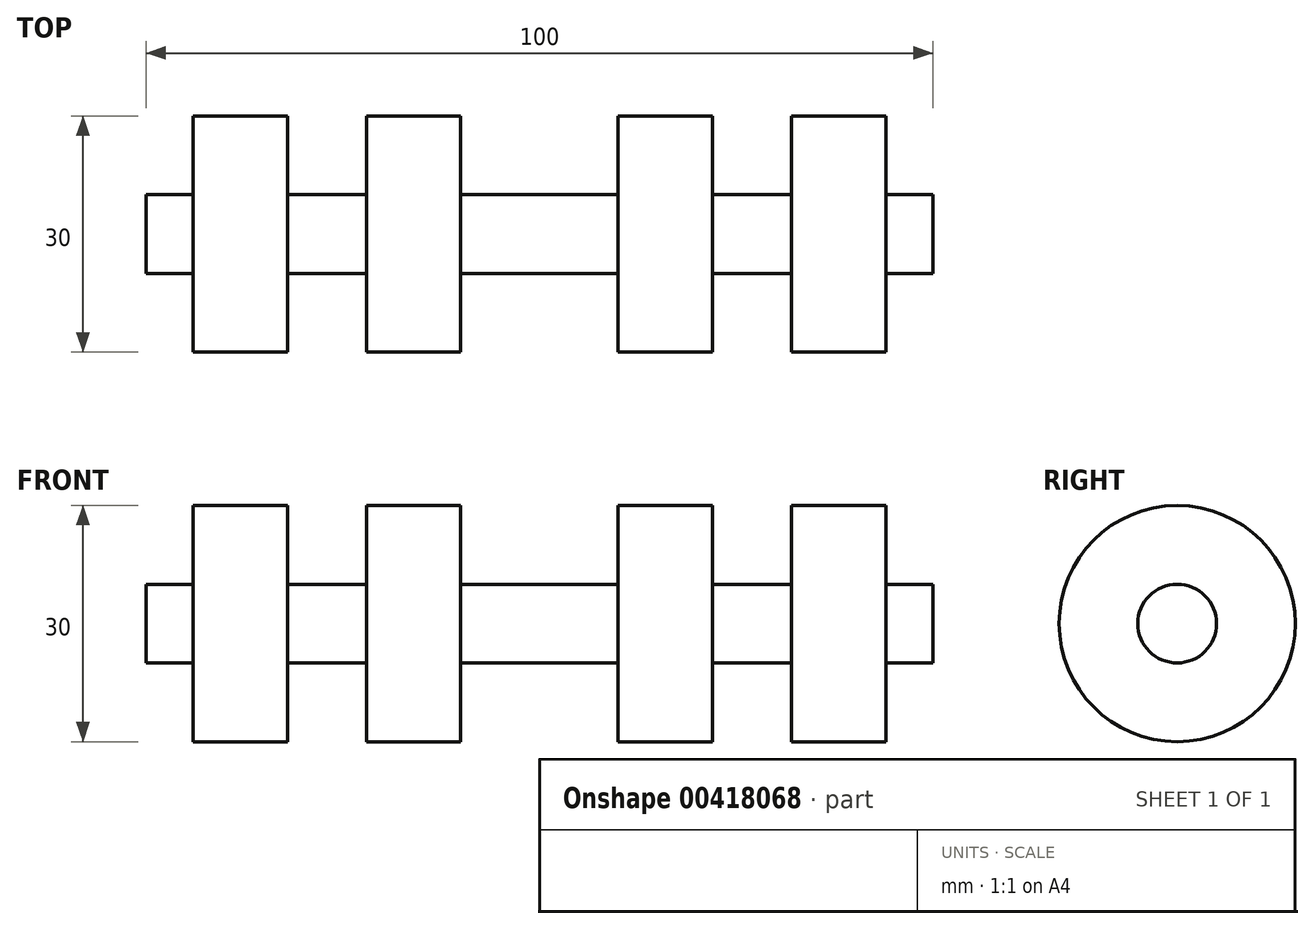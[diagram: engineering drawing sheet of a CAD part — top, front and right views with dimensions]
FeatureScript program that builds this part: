
annotation { "Feature Type Name" : "Feature", "Feature Type Description" : "" }
export const myFeature = defineFeature(function(context is Context, id is Id, definition is map)
    precondition{}
    {
        {
            var Q0;
            Q0=qCreatedBy(makeId("Front.planeOp"),FACE);
            var sketch = newSketch(context, id + "F0", { "sketchPlane" : qUnion([Q0])});
            skLineSegment(sketch, "E0.bottom", {"start": v(0, 0) * mm, "end": v(-100, 0) * mm});
            skLineSegment(sketch, "E0.top", {"start": v(-6, 15) * mm, "end": v(-18, 15) * mm});
            skLineSegment(sketch, "E0.left", {"start": v(0, 0) * mm, "end": v(0, 5) * mm});
            skLineSegment(sketch, "E0.right", {"start": v(-100, 0) * mm, "end": v(-100, 5) * mm});
            skLineSegment(sketch, "E1", {"start": v(-100, 5) * mm, "end": v(-94, 5) * mm});
            skLineSegment(sketch, "E2", {"start": v(-94, 15) * mm, "end": v(-94, 5) * mm});
            skLineSegment(sketch, "E3", {"start": v(-6, 15) * mm, "end": v(-6, 5) * mm});
            skLineSegment(sketch, "E4", {"start": v(-82, 15) * mm, "end": v(-82, 5) * mm});
            skLineSegment(sketch, "E5", {"start": v(-72, 15) * mm, "end": v(-72, 5) * mm});
            skLineSegment(sketch, "E6", {"start": v(-28, 15) * mm, "end": v(-28, 5) * mm});
            skLineSegment(sketch, "E7", {"start": v(-18, 15) * mm, "end": v(-18, 5) * mm});
            skLineSegment(sketch, "E8.trimOffspring", {"start": v(-6, 5) * mm, "end": v(0, 5) * mm});
            skLineSegment(sketch, "E9.trimOffspring", {"start": v(-28, 15) * mm, "end": v(-40, 15) * mm});
            skPoint(sketch, "E10.orphan", {"position": v(-18, 3.18) * mm});
            skPoint(sketch, "E11.orphan", {"position": v(-28, 3.18) * mm});
            skLineSegment(sketch, "E12.trimOffspring", {"start": v(-28, 5) * mm, "end": v(-18, 5) * mm});
            skPoint(sketch, "E13.orphan", {"position": v(-72, 3.18) * mm});
            skPoint(sketch, "E14.orphan", {"position": v(-82, 3.18) * mm});
            skLineSegment(sketch, "E15.trimOffspring", {"start": v(-82, 15) * mm, "end": v(-94, 15) * mm});
            skLineSegment(sketch, "E16.trimOffspring", {"start": v(-82, 5) * mm, "end": v(-72, 5) * mm});
            skLineSegment(sketch, "E17", {"start": v(13.67, 0) * mm, "end": v(-102.29, 0) * mm, "construction": true});
            skLineSegment(sketch, "E18", {"start": v(-60, 15) * mm, "end": v(-60, 5) * mm});
            skLineSegment(sketch, "E19", {"start": v(-40, 15) * mm, "end": v(-40, 5) * mm});
            skLineSegment(sketch, "E20.trimOffspring", {"start": v(-60, 15) * mm, "end": v(-72, 15) * mm});
            skLineSegment(sketch, "E21", {"start": v(-60, 5) * mm, "end": v(-40, 5) * mm});
            skSolve(sketch);
        }
        {
            var Q0;
            Q0=qSketchRegion(id+"F0",true);
            var Q1;
            Q1=sQuery(id+"F0.wireOp",EDGE,"E17");
            revolve(context, id + "F1", {"surfaceOperationType" : NewSurfaceOperationType.NEW, "entities" : qUnion([Q0]), "axis" : qUnion([Q1]), "revolveType" : RevolveType.FULL});
        }
    });
